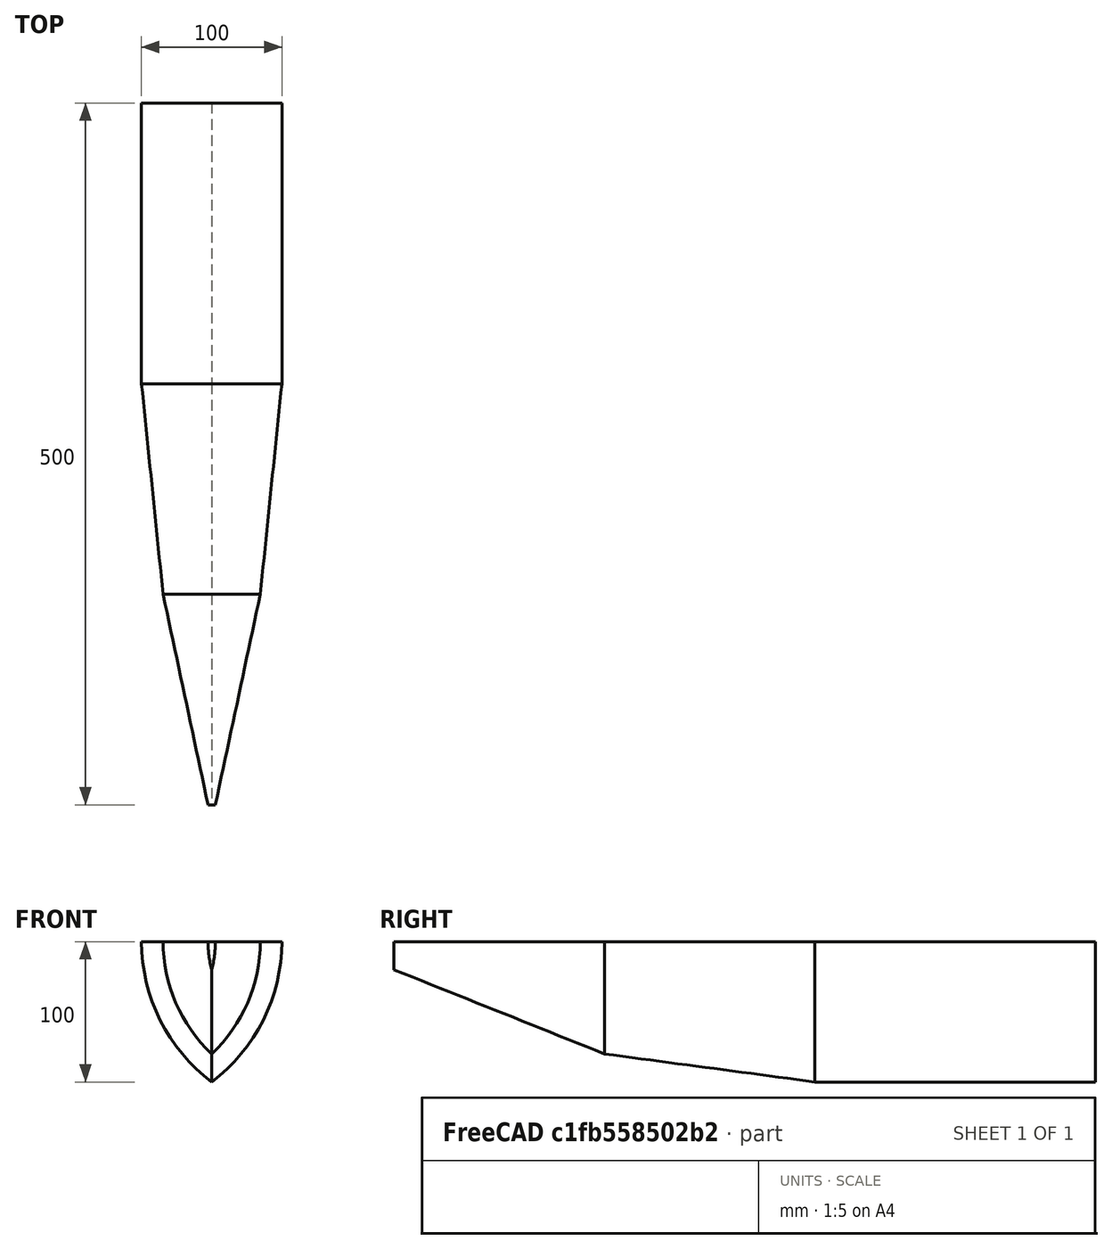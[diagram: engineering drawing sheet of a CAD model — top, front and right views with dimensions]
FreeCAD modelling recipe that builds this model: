
FCSTD DOCUMENT  (FreeCAD 0.20R29410 (Git))
Label: Casco_barco
License: All rights reserved
LicenseURL: http://en.wikipedia.org/wiki/All_rights_reserved
objects: Sketcher::SketchObject×4, PartDesign::Plane×3, PartDesign::AdditiveLoft×1, PartDesign::Body×1
note: 10 computed .brp shape members not serialized (recipe doc carries the construction recipe); baked Part::Feature solids carry a one-line shape summary decoded from their .brp

FEATURE [Sketcher::SketchObject] Sketch
  FullyConstrained = true
  MapMode = 5
  Placement = pos=(0,0,0) rot=(1,0,0;1.5708rad)
  Support = -> [XZ_Plane]
  sketch-geometry (3):
    g0: ArcOfCircle CenterX=75 CenterY=100 CenterZ=0 NormalX=0 NormalY=0 NormalZ=1 AngleXU=0 Radius=125 StartAngle=3.14159 EndAngle=4.06889
    g1: ArcOfCircle CenterX=-75 CenterY=100 CenterZ=0 NormalX=0 NormalY=0 NormalZ=1 AngleXU=0 Radius=125 StartAngle=5.35589 EndAngle=6.28319
    g2: LineSegment StartX=-50 StartY=100 StartZ=0 EndX=50 EndY=100 EndZ=0
  constraints (9):
    c: Horizontal(g0,g0)
    c: Coincident(g1,g0)
    c: DistanceX(g0,g1) = 100
    c: Symmetric(g0,g1,g-2)
    c: Coincident(g2,g0)
    c: Coincident(g2,g1)
    c: DistanceY(g0,g1) = 100
    c: Coincident(g0,g-1)
    c: Horizontal(g0,g1)
FEATURE [PartDesign::Plane] DatumPlane
  AttachmentOffset = pos=(0,0,350) rot=(0,0,1;0rad)
  Length = 122.361
  MapMode = 5
  Placement = pos=(0,-350,-7.77e-14) rot=(1,0,0;1.5708rad)
  ResizeMode = 0
  Support = -> [XZ_Plane]
  Width = 147.361
FEATURE [Sketcher::SketchObject] Sketch001
  ExternalGeometry = -> [Sketch]
  FullyConstrained = true
  MapMode = 5
  Placement = pos=(0,-350,-7.77e-14) rot=(1,0,0;1.5708rad)
  Support = -> [DatumPlane]
  sketch-geometry (3):
    g0: LineSegment StartX=-34.6586 StartY=100 StartZ=0 EndX=34.6586 EndY=100 EndZ=0
    g1: ArcOfCircle CenterX=75 CenterY=100 CenterZ=0 NormalX=0 NormalY=0 NormalZ=1 AngleXU=0 Radius=109.659 StartAngle=3.14159 EndAngle=3.95924
    g2: ArcOfCircle CenterX=-75 CenterY=100 CenterZ=0 NormalX=0 NormalY=0 NormalZ=1 AngleXU=0 Radius=109.659 StartAngle=5.46554 EndAngle=6.28319
  constraints (9):
    c: PointOnObject(g0,g-3)
    c: PointOnObject(g0,g-3)
    c: Coincident(g1,g-5)
    c: Coincident(g1,g0)
    c: PointOnObject(g1,g-2)
    c: Coincident(g2,g-4)
    c: Coincident(g2,g0)
    c: Coincident(g2,g1)
    c: DistanceY(g1,g0) = 80
FEATURE [PartDesign::Plane] DatumPlane001
  AttachmentOffset = pos=(0,0,500) rot=(0,0,1;0rad)
  Length = 122.361
  MapMode = 5
  Placement = pos=(0,-500,-1.11e-13) rot=(1,0,0;1.5708rad)
  ResizeMode = 0
  Support = -> [XZ_Plane]
  Width = 147.361
FEATURE [Sketcher::SketchObject] Sketch002
  ExternalGeometry = -> [Sketch]
  FullyConstrained = true
  MapMode = 5
  Placement = pos=(0,-500,-1.11e-13) rot=(1,0,0;1.5708rad)
  Support = -> [DatumPlane001]
  sketch-geometry (3):
    g0: LineSegment StartX=-2.62087 StartY=100 StartZ=0 EndX=2.62087 EndY=100 EndZ=0
    g1: ArcOfCircle CenterX=75 CenterY=100 CenterZ=0 NormalX=0 NormalY=0 NormalZ=1 AngleXU=0 Radius=77.6209 StartAngle=3.14159 EndAngle=3.4022
    g2: ArcOfCircle CenterX=-75 CenterY=100 CenterZ=0 NormalX=0 NormalY=0 NormalZ=1 AngleXU=0 Radius=77.6209 StartAngle=6.02258 EndAngle=6.28319
  constraints (9):
    c: PointOnObject(g0,g-3)
    c: PointOnObject(g0,g-3)
    c: Coincident(g1,g-5)
    c: Coincident(g1,g0)
    c: PointOnObject(g1,g-2)
    c: Coincident(g2,g-4)
    c: Coincident(g2,g0)
    c: Coincident(g2,g1)
    c: DistanceY(g1,g0) = 20
FEATURE [PartDesign::Plane] DatumPlane002
  AttachmentOffset = pos=(0,0,200) rot=(0,0,1;0rad)
  Length = 122.361
  MapMode = 5
  Placement = pos=(0,-200,-4.44e-14) rot=(1,0,0;1.5708rad)
  ResizeMode = 0
  Support = -> [XZ_Plane]
  Width = 147.361
FEATURE [Sketcher::SketchObject] Sketch003
  ExternalGeometry = -> [Sketch]
  FullyConstrained = true
  MapMode = 5
  Placement = pos=(0,-200,-4.44e-14) rot=(1,0,0;1.5708rad)
  Support = -> [DatumPlane002]
  sketch-geometry (3):
    g0: LineSegment StartX=-50 StartY=100 StartZ=0 EndX=50 EndY=100 EndZ=0
    g1: ArcOfCircle CenterX=75 CenterY=100 CenterZ=0 NormalX=0 NormalY=0 NormalZ=1 AngleXU=0 Radius=125 StartAngle=3.14159 EndAngle=4.06889
    g2: ArcOfCircle CenterX=-75 CenterY=100 CenterZ=0 NormalX=0 NormalY=0 NormalZ=1 AngleXU=0 Radius=125 StartAngle=5.35589 EndAngle=6.28319
  constraints (8):
    c: Coincident(g0,g-5)
    c: Coincident(g0,g-4)
    c: Coincident(g1,g-5)
    c: Coincident(g1,g0)
    c: Coincident(g1,g-5)
    c: Coincident(g2,g-4)
    c: Coincident(g2,g0)
    c: Coincident(g2,g1)
FEATURE [PartDesign::AdditiveLoft] AdditiveLoft
  Closed = false
  Placement = pos=(0,0,0) rot=(1,0,0;1.5708rad)
  Profile = -> Sketch
  Ruled = true
  Sections = -> [Sketch003,Sketch001,Sketch002]
FEATURE [PartDesign::Body] Body  label="Casco"
  Group = -> [Sketch,DatumPlane,Sketch001,DatumPlane001,Sketch002,DatumPlane002,Sketch003,AdditiveLoft]
  Origin = -> Origin
  Tip = -> AdditiveLoft
